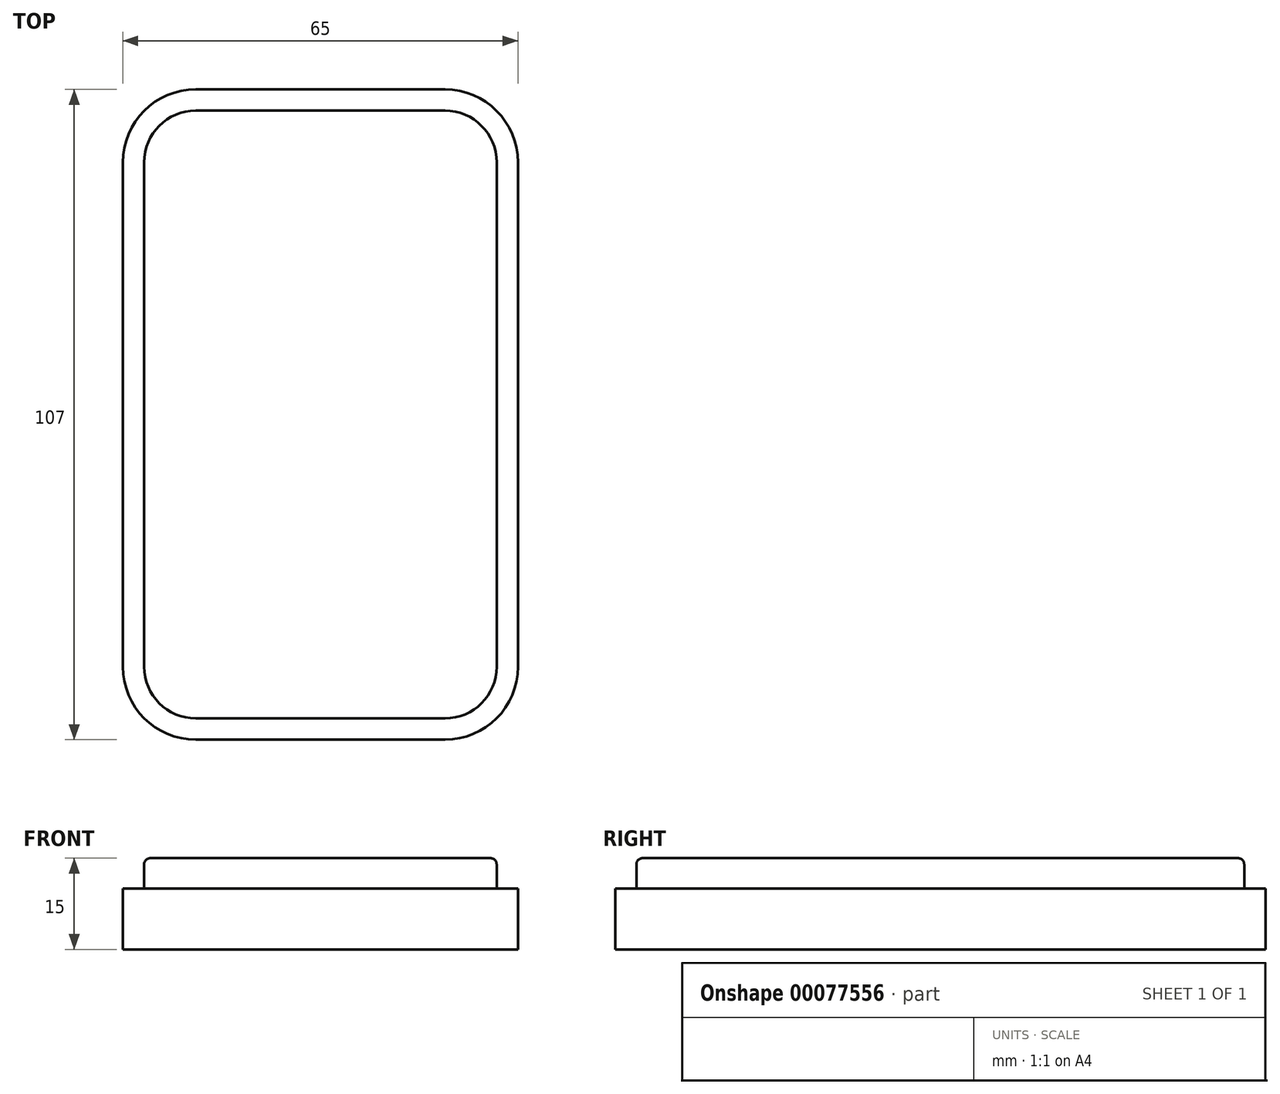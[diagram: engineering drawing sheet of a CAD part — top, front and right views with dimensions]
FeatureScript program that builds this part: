
annotation { "Feature Type Name" : "Feature", "Feature Type Description" : "" }
export const myFeature = defineFeature(function(context is Context, id is Id, definition is map)
    precondition{}
    {
        {
            var Q0;
            Q0=qCreatedBy(makeId("Top.planeOp"),FACE);
            var sketch = newSketch(context, id + "F0", { "sketchPlane" : qUnion([Q0])});
            skLineSegment(sketch, "E0.bottom", {"start": v(20.5, 53.5) * mm, "end": v(-20.5, 53.5) * mm});
            skLineSegment(sketch, "E0.top", {"start": v(20.5, -53.5) * mm, "end": v(-20.5, -53.5) * mm});
            skLineSegment(sketch, "E0.left", {"start": v(32.5, 41.5) * mm, "end": v(32.5, -41.5) * mm});
            skLineSegment(sketch, "E0.right", {"start": v(-32.5, 41.5) * mm, "end": v(-32.5, -41.5) * mm});
            skPoint(sketch, "E0.middle", {"position": v(0, 0) * mm});
            skPoint(sketch, "E1.visualSharp", {"position": v(-32.5, 53.5) * mm});
            skArc(sketch, "E1.filletArc", {"start": v(-20.5, 53.5) * mm, "mid": v(-28.99, 49.99) * mm, "end": v(-32.5, 41.5) * mm});
            skPoint(sketch, "E2.visualSharp", {"position": v(32.5, 53.5) * mm});
            skArc(sketch, "E2.filletArc", {"start": v(32.5, 41.5) * mm, "mid": v(28.99, 49.99) * mm, "end": v(20.5, 53.5) * mm});
            skPoint(sketch, "E3.visualSharp", {"position": v(32.5, -53.5) * mm});
            skArc(sketch, "E3.filletArc", {"start": v(20.5, -53.5) * mm, "mid": v(28.99, -49.99) * mm, "end": v(32.5, -41.5) * mm});
            skPoint(sketch, "E4.visualSharp", {"position": v(-32.5, -53.5) * mm});
            skArc(sketch, "E4.filletArc", {"start": v(-32.5, -41.5) * mm, "mid": v(-28.99, -49.99) * mm, "end": v(-20.5, -53.5) * mm});
            skPoint(sketch, "E5.visualSharp", {"position": v(-29, 50) * mm});
            skPoint(sketch, "E6.visualSharp", {"position": v(29, 50) * mm});
            skPoint(sketch, "E7.visualSharp", {"position": v(-29, -50) * mm});
            skPoint(sketch, "E8.visualSharp", {"position": v(29, -50) * mm});
            skArc(sketch, "E9.0", {"start": v(29, 41.5) * mm, "mid": v(26.51, 47.51) * mm, "end": v(20.5, 50) * mm});
            skLineSegment(sketch, "E9.1", {"start": v(29, 41.5) * mm, "end": v(29, -41.5) * mm});
            skLineSegment(sketch, "E9.2", {"start": v(20.5, 50) * mm, "end": v(-20.5, 50) * mm});
            skArc(sketch, "E9.3", {"start": v(20.5, -50) * mm, "mid": v(26.51, -47.51) * mm, "end": v(29, -41.5) * mm});
            skArc(sketch, "E9.4", {"start": v(-20.5, 50) * mm, "mid": v(-26.51, 47.51) * mm, "end": v(-29, 41.5) * mm});
            skLineSegment(sketch, "E9.5", {"start": v(-29, 41.5) * mm, "end": v(-29, -41.5) * mm});
            skArc(sketch, "E9.6", {"start": v(-29, -41.5) * mm, "mid": v(-26.51, -47.51) * mm, "end": v(-20.5, -50) * mm});
            skLineSegment(sketch, "E9.7", {"start": v(20.5, -50) * mm, "end": v(-20.5, -50) * mm});
            skSolve(sketch);
        }
        {
            var Q0;
            Q0=makeQuery(id+"F0.imprint","IMPRINT",FACE,{"disambiguationData":[TD([[makeQuery(id+"F0.imprint","IMPRINT",EDGE,{"derivedFrom":sQuery(id+"F0.wireOp",EDGE,"67ddf24b-318e-487f-bdd9-2af17ab4081c.0")}),-1.0]])]});
            var Q1;
            Q1=makeQuery(id+"F0.imprint","IMPRINT",FACE,{"disambiguationData":[TD([[makeQuery(id+"F0.imprint","IMPRINT",EDGE,{"derivedFrom":sQuery(id+"F0.wireOp",EDGE,"E9.0")}),1.0]])]});
            extrude(context, id + "F1", {"entities" : qUnion([Q0, Q1]), "depth" : 5 * mm});
        }
        {
            var Q0;
            Q0=qCreatedBy(makeId("Top.planeOp"),FACE);
            var sketch = newSketch(context, id + "F2", { "sketchPlane" : qUnion([Q0])});
            skLineSegment(sketch, "E10.bottom", {"start": v(20.5, 53.5) * mm, "end": v(-20.5, 53.5) * mm});
            skLineSegment(sketch, "E10.top", {"start": v(20.5, -53.5) * mm, "end": v(-20.5, -53.5) * mm});
            skLineSegment(sketch, "E10.left", {"start": v(32.5, 41.5) * mm, "end": v(32.5, -41.5) * mm});
            skLineSegment(sketch, "E10.right", {"start": v(-32.5, 41.5) * mm, "end": v(-32.5, -41.5) * mm});
            skPoint(sketch, "E10.middle", {"position": v(0, 0) * mm});
            skPoint(sketch, "E11.visualSharp", {"position": v(-32.5, 53.5) * mm});
            skArc(sketch, "E11.filletArc", {"start": v(-20.5, 53.5) * mm, "mid": v(-28.99, 49.99) * mm, "end": v(-32.5, 41.5) * mm});
            skPoint(sketch, "E12.visualSharp", {"position": v(32.5, 53.5) * mm});
            skArc(sketch, "E12.filletArc", {"start": v(32.5, 41.5) * mm, "mid": v(28.99, 49.99) * mm, "end": v(20.5, 53.5) * mm});
            skPoint(sketch, "E13.visualSharp", {"position": v(32.5, -53.5) * mm});
            skArc(sketch, "E13.filletArc", {"start": v(20.5, -53.5) * mm, "mid": v(28.99, -49.99) * mm, "end": v(32.5, -41.5) * mm});
            skPoint(sketch, "E14.visualSharp", {"position": v(-32.5, -53.5) * mm});
            skArc(sketch, "E14.filletArc", {"start": v(-32.5, -41.5) * mm, "mid": v(-28.99, -49.99) * mm, "end": v(-20.5, -53.5) * mm});
            skSolve(sketch);
        }
        {
            var Q0;
            Q0=makeQuery(id+"F2.imprint","IMPRINT",FACE,{"disambiguationData":[TD([[makeQuery(id+"F2.imprint","IMPRINT",EDGE,{"derivedFrom":sQuery(id+"F2.wireOp",EDGE,"E10.bottom")}),1.0]])]});
            extrude(context, id + "F3", {"entities" : qUnion([Q0]), "operationType" : NewBodyOperationType.ADD, "oppositeDirection" : true, "depth" : 10 * mm});
        }
        {
            var Q0;
            Q0=makeQuery(id+"F1.opExtrude","CAP_EDGE",EDGE,{"disambiguationData":[OSD([sQuery(id+"F0.wireOp",EDGE,"67ddf24b-318e-487f-bdd9-2af17ab4081c.4")])],"isStart":false});
            var Q1;
            Q1=makeQuery(id+"F1.opExtrude","CAP_EDGE",EDGE,{"disambiguationData":[OSD([sQuery(id+"F0.wireOp",EDGE,"67ddf24b-318e-487f-bdd9-2af17ab4081c.2")])],"isStart":false});
            var Q2;
            Q2=makeQuery(id+"F1.opExtrude","CAP_EDGE",EDGE,{"disambiguationData":[OSD([sQuery(id+"F0.wireOp",EDGE,"E9.2")])],"isStart":false});
            var Q3;
            Q3=makeQuery(id+"F1.opExtrude","CAP_EDGE",EDGE,{"disambiguationData":[OSD([sQuery(id+"F0.wireOp",EDGE,"E9.4")])],"isStart":false});
            var Q4;
            Q4=makeQuery(id+"F1.opExtrude","CAP_EDGE",EDGE,{"disambiguationData":[OSD([sQuery(id+"F0.wireOp",EDGE,"E9.5")])],"isStart":false});
            var Q5;
            Q5=makeQuery(id+"F1.opExtrude","CAP_EDGE",EDGE,{"disambiguationData":[OSD([sQuery(id+"F0.wireOp",EDGE,"E9.6")])],"isStart":false});
            var Q6;
            Q6=makeQuery(id+"F1.opExtrude","CAP_EDGE",EDGE,{"disambiguationData":[OSD([sQuery(id+"F0.wireOp",EDGE,"E9.7")])],"isStart":false});
            var Q7;
            Q7=makeQuery(id+"F1.opExtrude","CAP_EDGE",EDGE,{"disambiguationData":[OSD([sQuery(id+"F0.wireOp",EDGE,"E9.3")])],"isStart":false});
            var Q8;
            Q8=makeQuery(id+"F1.opExtrude","CAP_EDGE",EDGE,{"disambiguationData":[OSD([sQuery(id+"F0.wireOp",EDGE,"E9.1")])],"isStart":false});
            var Q9;
            Q9=makeQuery(id+"F1.opExtrude","CAP_EDGE",EDGE,{"disambiguationData":[OSD([sQuery(id+"F0.wireOp",EDGE,"E9.0")])],"isStart":false});
            fillet(context, id + "F4", {"entities" : qUnion([Q0, Q1, Q2, Q3, Q4, Q5, Q6, Q7, Q8, Q9]), "radius" : 1 * mm, "tangentPropagation" : true, "allowEdgeOverflow" : false});
        }
    });
